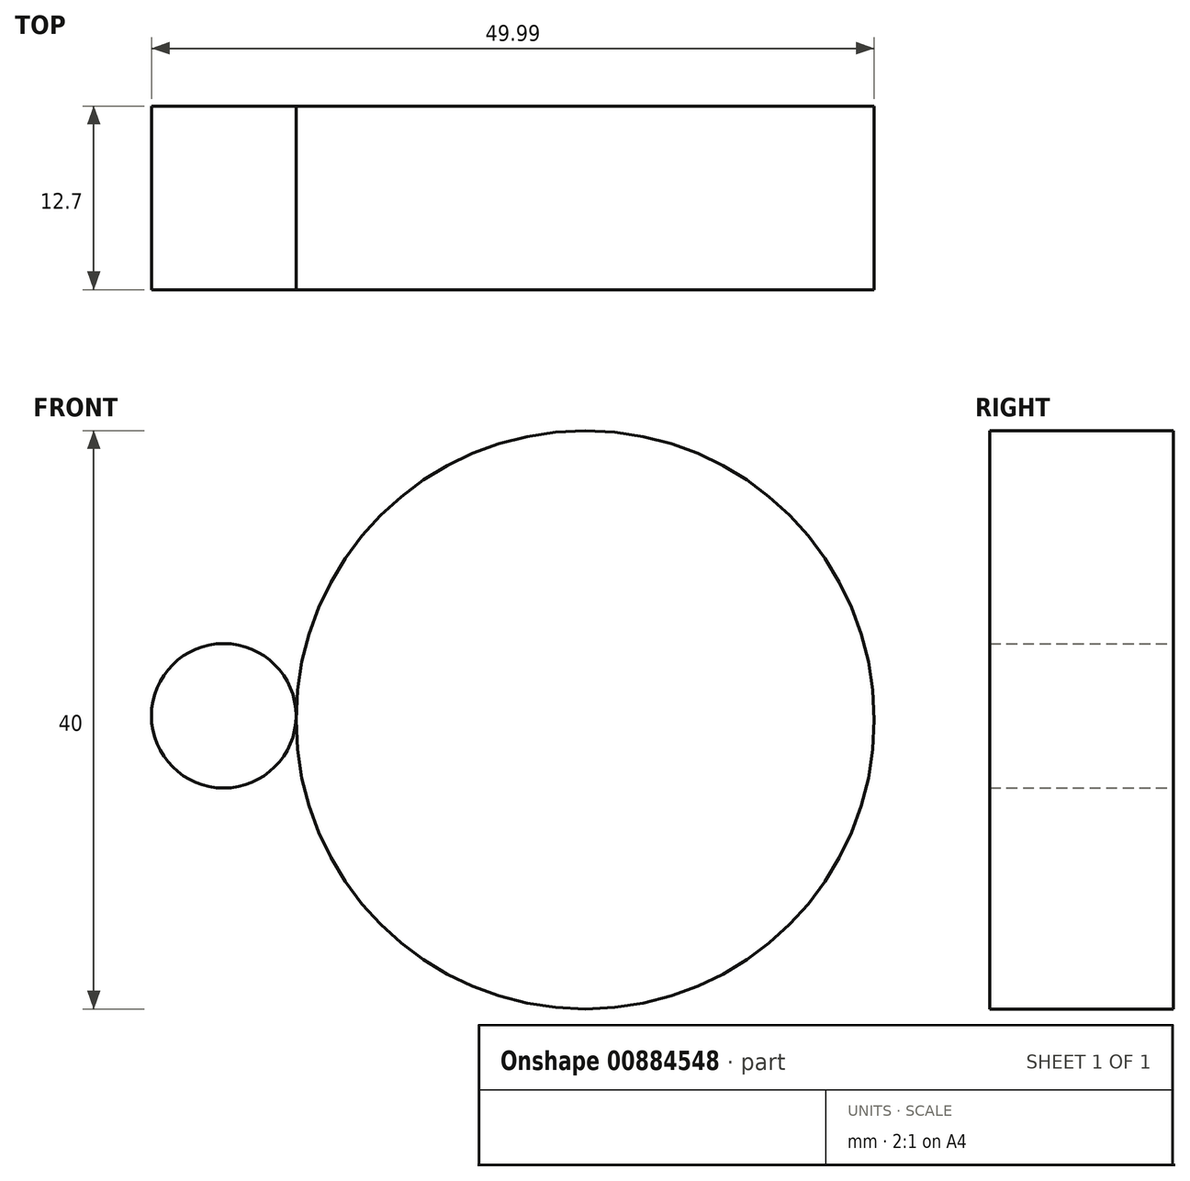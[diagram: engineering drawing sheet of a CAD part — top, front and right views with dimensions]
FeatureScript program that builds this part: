
annotation { "Feature Type Name" : "Feature", "Feature Type Description" : "" }
export const myFeature = defineFeature(function(context is Context, id is Id, definition is map)
    precondition{}
    {
        {
            var Q0;
            Q0=qCreatedBy(makeId("Front.planeOp"),FACE);
            var sketch = newSketch(context, id + "F0", { "sketchPlane" : qUnion([Q0])});
            skCircle(sketch, "E0", {"center": v(-41.9, 11.86) * mm, "radius": 5 * mm});
            skCircle(sketch, "E1", {"center": v(-16.9, 11.58) * mm, "radius": 20 * mm});
            skSolve(sketch);
        }
        {
            var Q0;
            Q0 = qSketchRegion(id + "F0", true);
            extrude(context, id + "F1", {"entities" : qUnion([Q0]), "depth" : 12.7 * mm, "offsetDistance" : 25.4 * mm});
        }
    });
